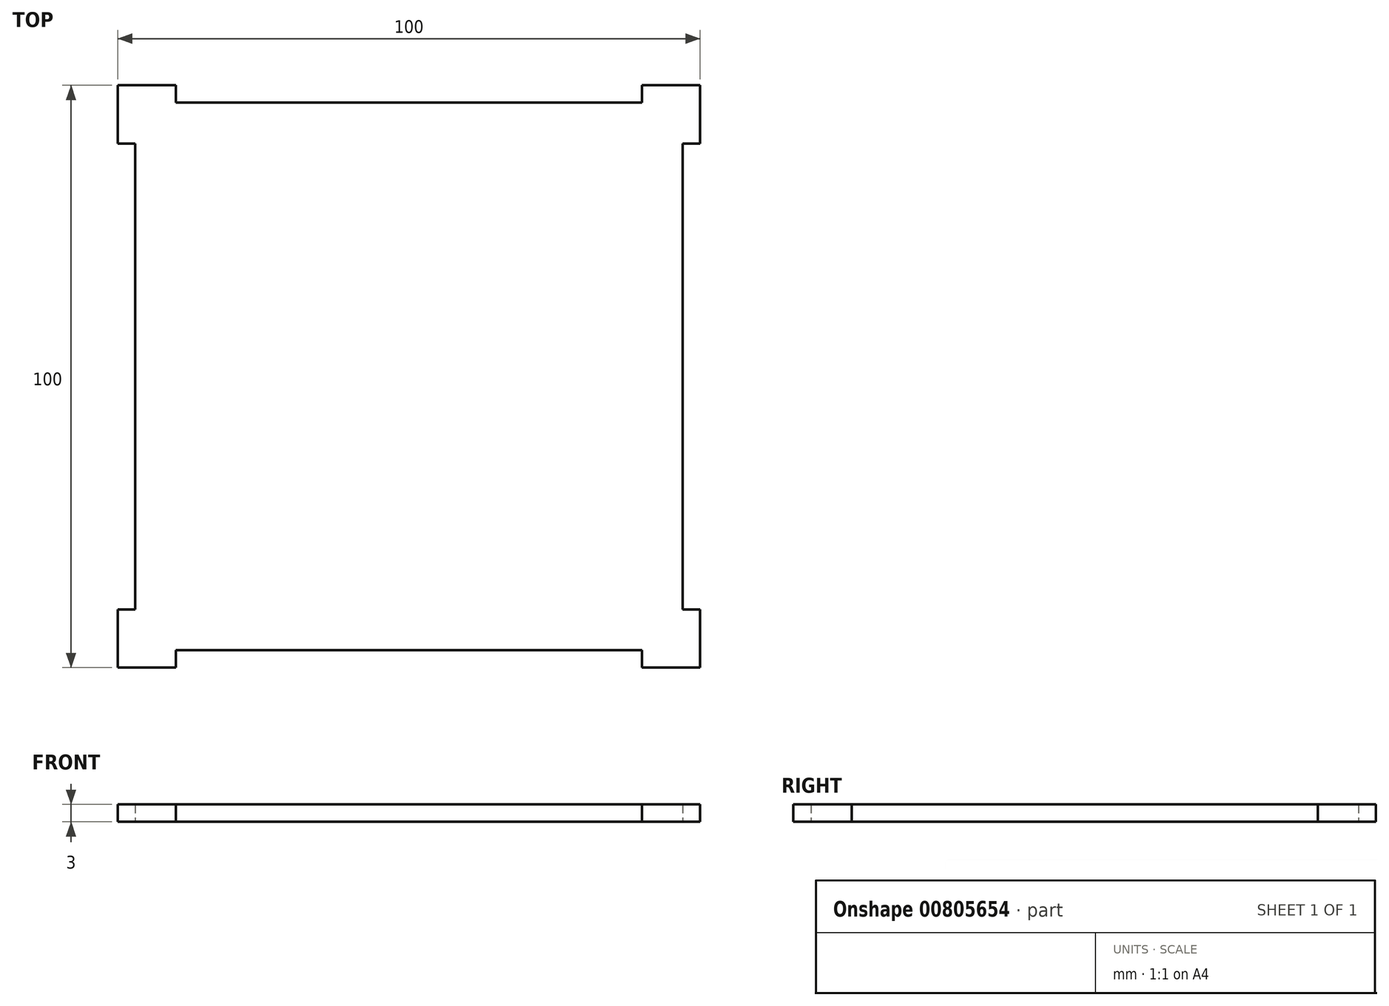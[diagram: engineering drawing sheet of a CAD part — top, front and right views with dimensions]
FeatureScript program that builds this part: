
annotation { "Feature Type Name" : "Feature", "Feature Type Description" : "" }
export const myFeature = defineFeature(function(context is Context, id is Id, definition is map)
    precondition{}
    {
        {
            var Q0;
            Q0=qCreatedBy(makeId("Top.planeOp"),FACE);
            var sketch = newSketch(context, id + "F0", { "sketchPlane" : qUnion([Q0])});
            skLineSegment(sketch, "E0.bottom", {"start": v(0, 0) * mm, "end": v(10, 0) * mm});
            skLineSegment(sketch, "E0.top", {"start": v(0, 100) * mm, "end": v(10, 100) * mm});
            skLineSegment(sketch, "E0.left", {"start": v(0, 0) * mm, "end": v(0, 10) * mm});
            skLineSegment(sketch, "E0.right", {"start": v(100, 0) * mm, "end": v(100, 10) * mm});
            skLineSegment(sketch, "E1", {"start": v(3, 50) * mm, "end": v(97, 50) * mm, "construction": true});
            skLineSegment(sketch, "E2", {"start": v(50, 97) * mm, "end": v(50, 3) * mm, "construction": true});
            skLineSegment(sketch, "E3", {"start": v(10, 97) * mm, "end": v(90, 97) * mm});
            skLineSegment(sketch, "E4", {"start": v(10, 97) * mm, "end": v(10, 100) * mm});
            skLineSegment(sketch, "E5", {"start": v(90, 97) * mm, "end": v(90, 100) * mm});
            skLineSegment(sketch, "E6.trimOffspring", {"start": v(90, 100) * mm, "end": v(100, 100) * mm});
            skLineSegment(sketch, "E7.MirrorCS", {"start": v(10, 3) * mm, "end": v(90, 3) * mm});
            skLineSegment(sketch, "E8.MirrorCS", {"start": v(10, 3) * mm, "end": v(10, 0) * mm});
            skLineSegment(sketch, "E9.MirrorCS", {"start": v(90, 3) * mm, "end": v(90, 0) * mm});
            skLineSegment(sketch, "E10.trimOffspring", {"start": v(90, 0) * mm, "end": v(100, 0) * mm});
            skLineSegment(sketch, "E11", {"start": v(3, 90) * mm, "end": v(3, 10) * mm});
            skLineSegment(sketch, "E12", {"start": v(3, 90) * mm, "end": v(0, 90) * mm});
            skLineSegment(sketch, "E13", {"start": v(3, 10) * mm, "end": v(0, 10) * mm});
            skLineSegment(sketch, "E14.trimOffspring", {"start": v(0, 90) * mm, "end": v(0, 100) * mm});
            skPoint(sketch, "E15.orphan", {"position": v(0, 50) * mm});
            skLineSegment(sketch, "E16.MirrorCS", {"start": v(97, 90) * mm, "end": v(100, 90) * mm});
            skLineSegment(sketch, "E17.MirrorCS", {"start": v(97, 90) * mm, "end": v(97, 10) * mm});
            skLineSegment(sketch, "E18.MirrorCS", {"start": v(97, 10) * mm, "end": v(100, 10) * mm});
            skLineSegment(sketch, "E19.trimOffspring", {"start": v(100, 90) * mm, "end": v(100, 100) * mm});
            skPoint(sketch, "E20.orphan", {"position": v(100, 50) * mm});
            skSolve(sketch);
        }
        {
            var Q0;
            Q0=makeQuery(id+"F0.imprint","IMPRINT",FACE,{"disambiguationData":[TD([[makeQuery(id+"F0.imprint","IMPRINT",EDGE,{"derivedFrom":sQuery(id+"F0.wireOp",EDGE,"E0.bottom")}),1.0]])]});
            extrude(context, id + "F1", {"entities" : qUnion([Q0]), "depth" : 3 * mm, "offsetDistance" : 25 * mm});
        }
    });
